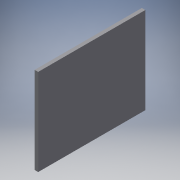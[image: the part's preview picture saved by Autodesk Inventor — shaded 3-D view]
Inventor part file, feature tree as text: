
AUTODESK INVENTOR PART (.ipt)
format: ipt  version: 2017 (Build 210142000, 142)  size: 95,232 bytes
history: native  units: mm
features: extrude x1, sketch x1
ambient origin geometry x8: Origin, YZ Plane, XZ Plane, XY Plane, X Axis, Y Axis, Z Axis, Center Point
bodies: Solid1 (feature_tree)
feature tree (2):
  extrude  "Extrusion1"  [1 undecoded]
  sketch  "Sketch1"  dims[d0=361.75mm d1=0.0mm]
note: 1 required parameter value undecoded (feature->parameter linkage not recoverable at this tier; creation-order binding heuristic only, values carry confidence <= 0.55)
